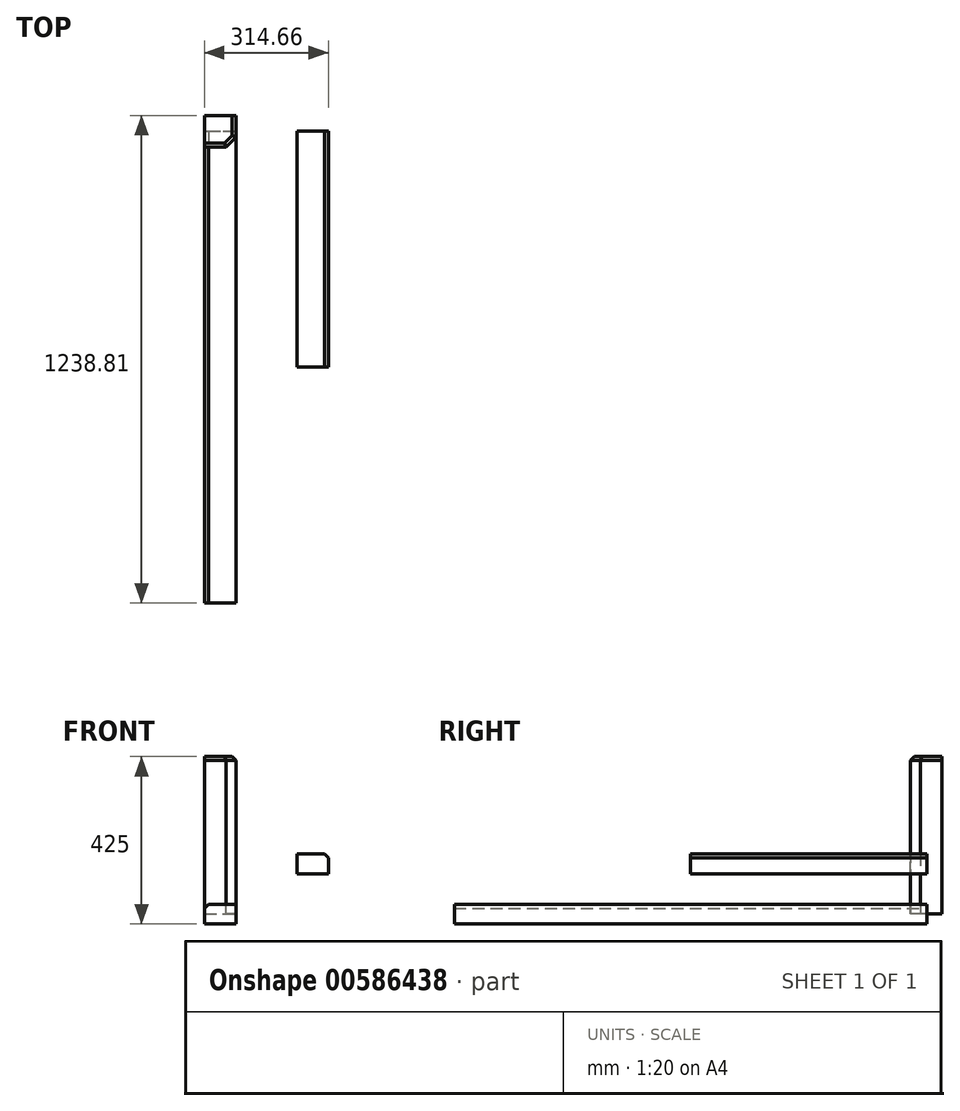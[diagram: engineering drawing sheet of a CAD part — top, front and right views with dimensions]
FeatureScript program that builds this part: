
annotation { "Feature Type Name" : "Feature", "Feature Type Description" : "" }
export const myFeature = defineFeature(function(context is Context, id is Id, definition is map)
    precondition{}
    {
        {
            var Q0;
            Q0=qCreatedBy(makeId("Top.planeOp"),FACE);
            var sketch = newSketch(context, id + "F0", { "sketchPlane" : qUnion([Q0])});
            skLineSegment(sketch, "E0.bottom", {"start": v(-40.39, 38.81) * mm, "end": v(39.61, 38.81) * mm});
            skLineSegment(sketch, "E0.top", {"start": v(-40.39, -41.19) * mm, "end": v(39.61, -41.19) * mm});
            skLineSegment(sketch, "E0.left", {"start": v(-40.39, 38.81) * mm, "end": v(-40.39, -41.19) * mm});
            skLineSegment(sketch, "E0.right", {"start": v(39.61, 38.81) * mm, "end": v(39.61, -41.19) * mm});
            skSolve(sketch);
        }
        {
            var Q0;
            Q0=makeQuery(id+"F0.imprint","IMPRINT",FACE,{"disambiguationData":[TD([[makeQuery(id+"F0.imprint","IMPRINT",EDGE,{"derivedFrom":sQuery(id+"F0.wireOp",EDGE,"E0.bottom")}),-1.0]])]});
            extrude(context, id + "F1", {"entities" : qUnion([Q0]), "depth" : 400 * mm, "offsetDistance" : 25 * mm});
        }
        {
            var Q0;
            Q0=makeQuery(id+"F1.opExtrude","SWEPT_EDGE",EDGE,{"disambiguationData":[OSD([sQuery(id+"F0.wireOp",EDGE,"E0.top"),sQuery(id+"F0.wireOp",EDGE,"E0.right")])]});
            chamfer(context, id + "F2", {"entities" : qUnion([Q0]), "width" : 25 * mm, "tangentPropagation" : true});
        }
        {
            var Q0;
            Q0=makeQuery(id+"F1.opExtrude","CAP_EDGE",EDGE,{"disambiguationData":[OSD([sQuery(id+"F0.wireOp",EDGE,"E0.top")])],"isStart":false});
            var Q1;
            Q1=makeQuery(id+"F1.opExtrude","CAP_EDGE",EDGE,{"disambiguationData":[OSD([sQuery(id+"F0.wireOp",EDGE,"E0.right")])],"isStart":false});
            var Q2;
            {var subQ0=sQuery(id+"F0.wireOp",EDGE,"E0.right");var subQ1=sQuery(id+"F0.wireOp",EDGE,"E0.top");Q2=makeQuery(id+"F2.opChamfer","BLEND_EDGE",EDGE,{"blendedFrom":[makeQuery(id+"F1.opExtrude","SWEPT_EDGE",EDGE,{"disambiguationData":[OSD([subQ1,subQ0])]}),makeQuery(id+"F1.opExtrude","CAP_FACE",FACE,{"disambiguationData":[OSD([sQuery(id+"F0.wireOp",EDGE,"E0.bottom"),subQ1,sQuery(id+"F0.wireOp",EDGE,"E0.left"),subQ0])],"isStart":false})],"blendedInto":[makeQuery(id+"F1.opExtrude","CAP_FACE",FACE,{"disambiguationData":[OSD([sQuery(id+"F0.wireOp",EDGE,"E0.bottom"),subQ1,sQuery(id+"F0.wireOp",EDGE,"E0.left"),subQ0])],"isStart":false})]});}
            chamfer(context, id + "F3", {"entities" : qUnion([Q0, Q1, Q2]), "width" : 10 * mm, "tangentPropagation" : true});
        }
        {
            var Q0;
            Q0=qCreatedBy(makeId("Front.planeOp"),FACE);
            var sketch = newSketch(context, id + "F4", { "sketchPlane" : qUnion([Q0])});
            skLineSegment(sketch, "E1.bottom", {"start": v(194.27, 152.41) * mm, "end": v(274.27, 152.41) * mm});
            skLineSegment(sketch, "E1.top", {"start": v(194.27, 102.41) * mm, "end": v(274.27, 102.41) * mm});
            skLineSegment(sketch, "E1.left", {"start": v(194.27, 152.41) * mm, "end": v(194.27, 102.41) * mm});
            skLineSegment(sketch, "E1.right", {"start": v(274.27, 152.41) * mm, "end": v(274.27, 102.41) * mm});
            skSolve(sketch);
        }
        {
            var Q0;
            Q0=makeQuery(id+"F4.imprint","IMPRINT",FACE,{"disambiguationData":[TD([[makeQuery(id+"F4.imprint","IMPRINT",EDGE,{"derivedFrom":sQuery(id+"F4.wireOp",EDGE,"E1.bottom")}),-1.0]])]});
            extrude(context, id + "F5", {"entities" : qUnion([Q0]), "depth" : 600 * mm, "offsetDistance" : 25 * mm});
        }
        {
            var Q0;
            Q0=qCreatedBy(makeId("Front.planeOp"),FACE);
            var sketch = newSketch(context, id + "F6", { "sketchPlane" : qUnion([Q0])});
            skLineSegment(sketch, "E2.bottom", {"start": v(-40, 25) * mm, "end": v(40, 25) * mm});
            skLineSegment(sketch, "E2.top", {"start": v(-40, -25) * mm, "end": v(40, -25) * mm});
            skLineSegment(sketch, "E2.left", {"start": v(-40, 25) * mm, "end": v(-40, -25) * mm});
            skLineSegment(sketch, "E2.right", {"start": v(40, 25) * mm, "end": v(40, -25) * mm});
            skSolve(sketch);
        }
        {
            var Q0;
            Q0 = qSketchRegion(id + "F6", true);
            extrude(context, id + "F7", {"entities" : qUnion([Q0]), "depth" : 1200 * mm, "offsetDistance" : 25 * mm});
        }
        {
            var Q0;
            Q0=makeQuery(id+"F5.opExtrude","SWEPT_EDGE",EDGE,{"disambiguationData":[OSD([sQuery(id+"F4.wireOp",EDGE,"E1.bottom"),sQuery(id+"F4.wireOp",EDGE,"E1.right")])]});
            chamfer(context, id + "F8", {"entities" : qUnion([Q0]), "width" : 10 * mm, "tangentPropagation" : true});
        }
        {
            var Q0;
            Q0=makeQuery(id+"F7.opExtrude","SWEPT_EDGE",EDGE,{"disambiguationData":[OSD([sQuery(id+"F6.wireOp",EDGE,"E2.bottom"),sQuery(id+"F6.wireOp",EDGE,"E2.left")])]});
            chamfer(context, id + "F9", {"entities" : qUnion([Q0]), "width" : 10 * mm, "tangentPropagation" : true});
        }
    });
